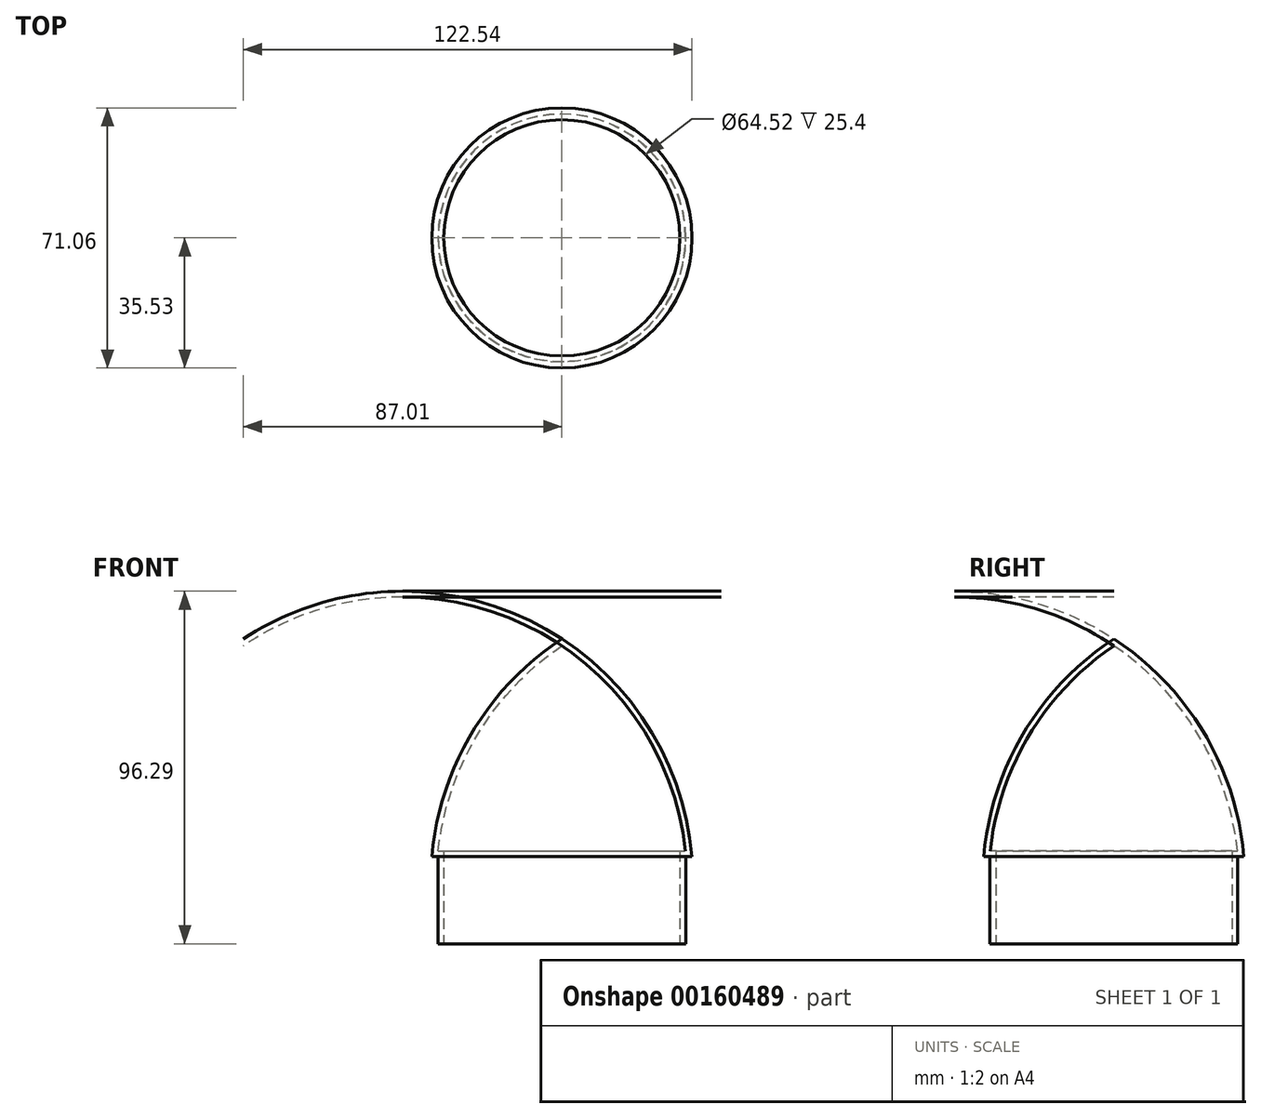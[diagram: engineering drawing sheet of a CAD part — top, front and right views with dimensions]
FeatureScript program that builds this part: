
annotation { "Feature Type Name" : "Feature", "Feature Type Description" : "" }
export const myFeature = defineFeature(function(context is Context, id is Id, definition is map)
    precondition{}
    {
        {
            var Q0;
            Q0=qCreatedBy(makeId("Front.planeOp"),FACE);
            var sketch = newSketch(context, id + "F0", { "sketchPlane" : qUnion([Q0])});
            skLineSegment(sketch, "E0", {"start": v(0, 0) * mm, "end": v(0, 101.6) * mm});
            skLineSegment(sketch, "E1", {"start": v(32.26, 20.2) * mm, "end": v(32.26, 45.6) * mm});
            skLineSegment(sketch, "E2", {"start": v(32.26, 45.6) * mm, "end": v(33.78, 45.6) * mm});
            skArc(sketch, "E3", {"start": v(33.78, 45.6) * mm, "mid": v(23.06, 77.33) * mm, "end": v(0, 101.6) * mm});
            skArc(sketch, "E4.0", {"start": v(35.53, 44.02) * mm, "mid": v(24.6, 77.85) * mm, "end": v(0, 103.5) * mm});
            skLineSegment(sketch, "E4.1", {"start": v(33.85, 44.02) * mm, "end": v(35.53, 44.02) * mm});
            skLineSegment(sketch, "E4.2", {"start": v(33.85, 20.2) * mm, "end": v(33.85, 44.02) * mm});
            skLineSegment(sketch, "E5", {"start": v(32.26, 20.2) * mm, "end": v(33.85, 20.2) * mm});
            skLineSegment(sketch, "E6", {"start": v(0, 101.6) * mm, "end": v(0, 103.5) * mm});
            skLineSegment(sketch, "E7", {"start": v(32.26, 29.46) * mm, "end": v(27.7, 29.46) * mm});
            skLineSegment(sketch, "E8", {"start": v(27.7, 29.46) * mm, "end": v(27.7, 35.8) * mm});
            skLineSegment(sketch, "E9", {"start": v(27.7, 33.72) * mm, "end": v(29.84, 33.72) * mm});
            skSolve(sketch);
        }
        {
            var Q0;
            Q0 = qSketchRegion(id + "F0", true);
            var Q1;
            Q1=sQuery(id+"F0.wireOp",EDGE,"E0");
            revolve(context, id + "F1", {"entities" : qUnion([Q0]), "axis" : qUnion([Q1]), "revolveType" : RevolveType.FULL});
        }
    });
